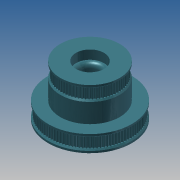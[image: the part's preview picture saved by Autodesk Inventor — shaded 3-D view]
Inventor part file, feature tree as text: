
AUTODESK INVENTOR PART (.ipt)
format: ipt  version: 2013 (Build 170138000, 138)  size: 1,191,424 bytes
history: native  units: mm
features: extrude x11, sketch x11, pattern_circular x2, chamfer x1, fillet x1
ambient origin geometry x8: Origin, YZ Plane, XZ Plane, XY Plane, X Axis, Y Axis, Z Axis, Center Point
bodies: Solid1 (feature_tree)
feature tree (26):
  extrude  "Extrusion1"  Depth=8.0mm TaperAngle=0.0deg
  extrude  "Extrusion2"  Depth=8.0mm TaperAngle=0.0deg
  pattern_circular  "Circular Pattern1"  Count=70 Angle=360.0deg
  extrude  "Extrusion3"  Depth=2.5mm TaperAngle=0.0deg
  extrude  "Extrusion4"  Depth=63.661977mm
  extrude  "Extrusion5"  Depth=1.59mm
  extrude  "Extrusion6"  Depth=1000.0mm TaperAngle=360.0deg
  pattern_circular  "Circular Pattern2"  [2 undecoded]
  extrude  "Extrusion7"  Depth=22.0mm
  extrude  "Extrusion8"  Depth=7.0mm TaperAngle=0.0deg
  chamfer  "Chamfer1"  Distance=7.0mm
  extrude  "Extrusion9"  Depth=3.5mm
  extrude  "Extrusion10"  [1 undecoded]
  extrude  "Extrusion11"  [1 undecoded]
  fillet  "Fillet1"  [1 undecoded]
  sketch  "Sketch1"  dims[d0=44.563384mm d2=8.0mm d3=0.0mm]
  sketch  "Sketch2"  dims[d4=1.59mm d6=8.0mm d7=0.0mm d8=700.0mm d9=360.0deg]
  sketch  "Sketch3"  dims[d11=1.0mm d12=2.5mm d13=0.0mm]
  sketch  "Sketch4"  dims[d14=16.1mm d15=0.0mm d16=63.661977mm]
  sketch  "Sketch5"  dims[d18=13.0mm d19=0.0mm d20=1.59mm]
  sketch  "Sketch6"  dims[d22=13.0mm d23=0.0mm d24=1000.0mm d25=360.0deg]
  sketch  "Sketch7"  dims[d27=1.0mm]
  sketch  "Sketch8"  dims[d28=2.5mm d29=0.0mm]
  sketch  "Sketch9"  dims[d30=2.5mm d31=0.0mm]
  sketch  "Sketch10"  dims[d32=1.0mm d33=2.0mm d34=45.0deg]
  sketch  "Sketch11"  dims[d35=15.0mm d37=2.5mm d38=0.0mm d39=22.0mm d41=7.0mm d42=0.0mm d43=7.0mm d44=0.0mm d45=3.5mm]
note: 5 required parameter values undecoded (feature->parameter linkage not recoverable at this tier; creation-order binding heuristic only, values carry confidence <= 0.55)
